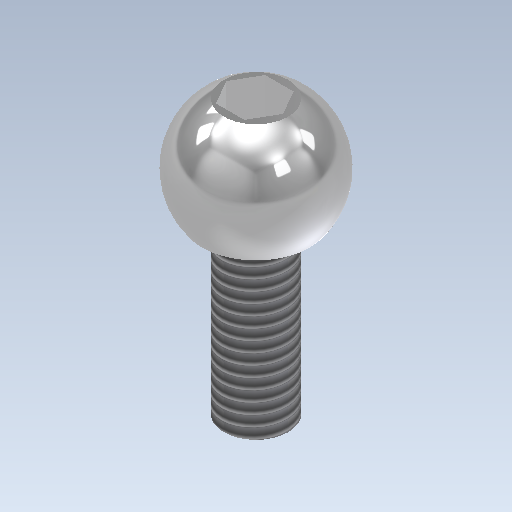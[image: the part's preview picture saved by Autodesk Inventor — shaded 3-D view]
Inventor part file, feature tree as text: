
AUTODESK INVENTOR PART (.ipt)
format: ipt  version: 2020 (Build 240168000, 168)  size: 181,760 bytes
history: native  units: mm
features: sketch x4, extrude x3, revolve x1, thread x1, projected_geometry x1
ambient origin geometry x8: Origin, YZ Plane, XZ Plane, XY Plane, X Axis, Y Axis, Z Axis, Center Point
bodies: Solid1 (feature_tree)
feature tree (10):
  revolve  "Revolution1"  Angle=90.0deg
  extrude  "Extrusion1"  Depth=10.0mm TaperAngle=0.0deg
  extrude  "Extrusion2"  Depth=8.0mm TaperAngle=0.0deg
  thread  "Thread1"  [1 undecoded]
  extrude  "Extrusion3"  Depth=2.0mm TaperAngle=0.0deg
  sketch  "Sketch1"  dims[d0=6.4mm d1=90.0deg]
  sketch  "Sketch2"  dims[d2=4.8mm d3=10.0mm d4=0.0mm]
  sketch  "Sketch3"  dims[d5=3.0mm d6=8.0mm d7=0.0mm d8=3.0mm]
  sketch  "Sketch4"  dims[d9=10.0mm d10=0.0mm d11=2.0mm d12=0.0mm]
  projected_geometry  "Project Cut Edges1"
note: 1 required parameter value undecoded (feature->parameter linkage not recoverable at this tier; creation-order binding heuristic only, values carry confidence <= 0.55)
